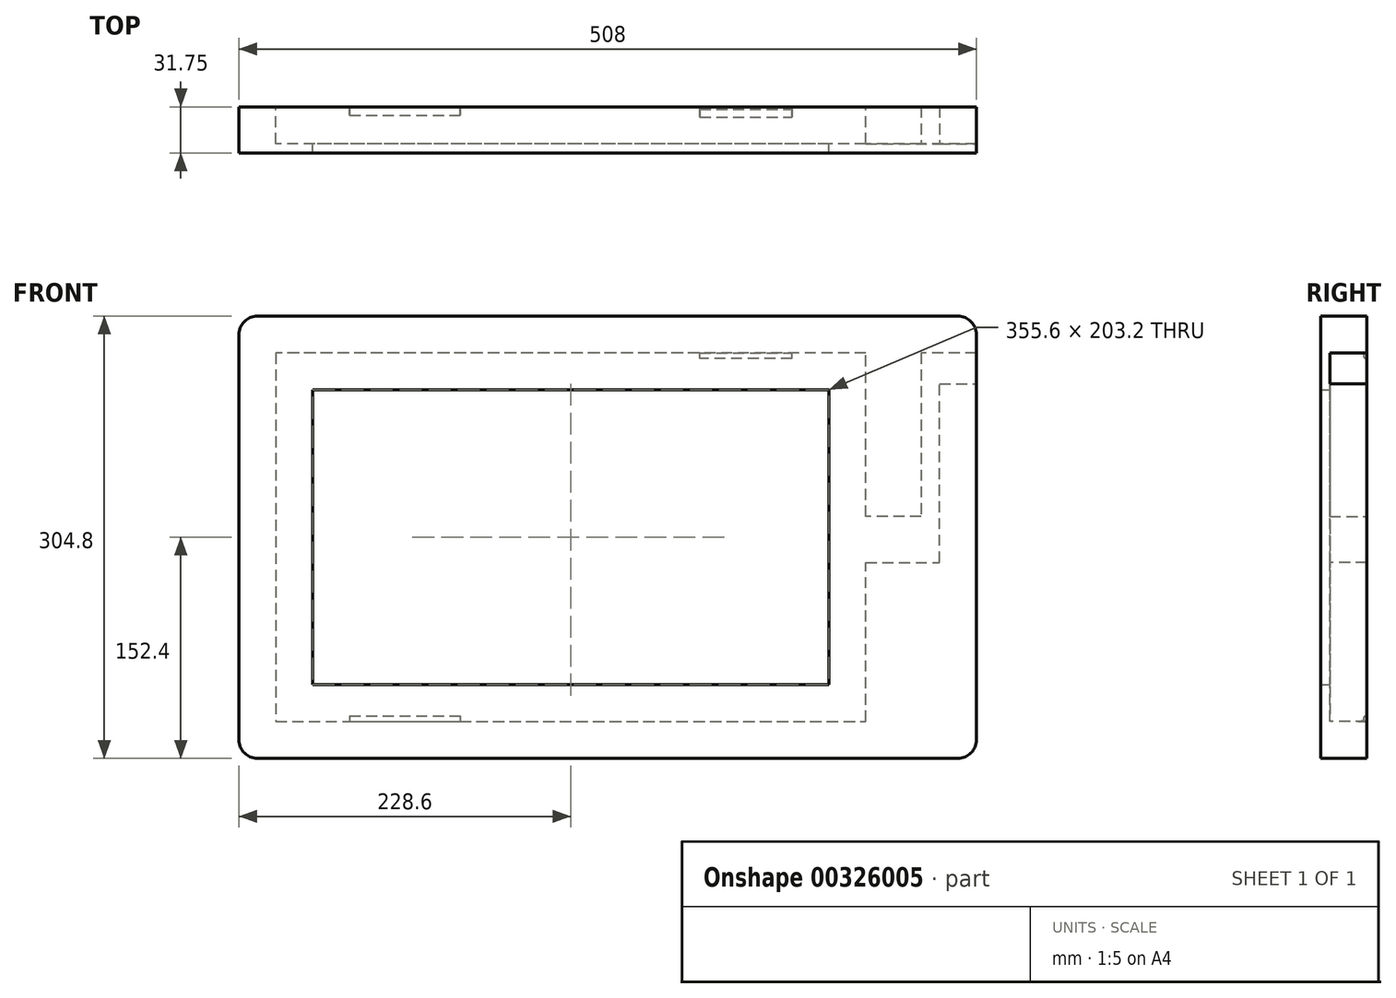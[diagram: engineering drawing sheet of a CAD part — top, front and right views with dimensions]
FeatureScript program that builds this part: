
annotation { "Feature Type Name" : "Feature", "Feature Type Description" : "" }
export const myFeature = defineFeature(function(context is Context, id is Id, definition is map)
    precondition{}
    {
        {
            var Q0;
            Q0=qCreatedBy(makeId("Front.planeOp"),FACE);
            var sketch = newSketch(context, id + "F0", { "sketchPlane" : qUnion([Q0])});
            skLineSegment(sketch, "E0.bottom", {"start": v(177.8, -101.6) * mm, "end": v(-177.8, -101.6) * mm});
            skLineSegment(sketch, "E0.top", {"start": v(177.8, 101.6) * mm, "end": v(-177.8, 101.6) * mm});
            skLineSegment(sketch, "E0.left", {"start": v(177.8, -101.6) * mm, "end": v(177.8, 101.6) * mm});
            skLineSegment(sketch, "E0.right", {"start": v(-177.8, -101.6) * mm, "end": v(-177.8, 101.6) * mm});
            skPoint(sketch, "E0.middle", {"position": v(0, 0) * mm});
            skLineSegment(sketch, "E1.bottom", {"start": v(203.2, 127) * mm, "end": v(-203.2, 127) * mm});
            skLineSegment(sketch, "E1.top", {"start": v(203.2, -127) * mm, "end": v(-203.2, -127) * mm});
            skLineSegment(sketch, "E1.left", {"start": v(203.2, 127) * mm, "end": v(203.2, -127) * mm});
            skLineSegment(sketch, "E1.right", {"start": v(-203.2, 127) * mm, "end": v(-203.2, -127) * mm});
            skLineSegment(sketch, "E2.bottom", {"start": v(279.4, -152.4) * mm, "end": v(-228.6, -152.4) * mm});
            skLineSegment(sketch, "E2.top", {"start": v(279.4, 152.4) * mm, "end": v(-228.6, 152.4) * mm});
            skLineSegment(sketch, "E2.left", {"start": v(279.4, -152.4) * mm, "end": v(279.4, 152.4) * mm});
            skPoint(sketch, "E3.oppositeSnap0", {"position": v(203.2, 0) * mm});
            skLineSegment(sketch, "E3.bottom", {"start": v(241.3, 152.4) * mm, "end": v(254, 152.4) * mm});
            skLineSegment(sketch, "E3.left", {"start": v(241.3, 127) * mm, "end": v(241.3, 14.4) * mm});
            skLineSegment(sketch, "E3.right", {"start": v(254, 105.83) * mm, "end": v(254, 0) * mm});
            skLineSegment(sketch, "E4.bottom", {"start": v(173.05, 14.4) * mm, "end": v(241.3, 14.4) * mm});
            skLineSegment(sketch, "E4.top", {"start": v(173.05, -17.34) * mm, "end": v(254, -17.34) * mm});
            skLineSegment(sketch, "E4.left", {"start": v(173.05, 14.4) * mm, "end": v(173.05, -17.34) * mm});
            skLineSegment(sketch, "E5", {"start": v(254, 0) * mm, "end": v(254, -17.34) * mm});
            skLineSegment(sketch, "E6", {"start": v(241.3, 127) * mm, "end": v(279.4, 127) * mm});
            skLineSegment(sketch, "E7", {"start": v(254, 105.83) * mm, "end": v(279.4, 105.83) * mm});
            skLineSegment(sketch, "E8", {"start": v(-228.6, 152.4) * mm, "end": v(-228.6, -152.4) * mm});
            skPoint(sketch, "E2.right.end.orphan", {"position": v(-279.4, 152.4) * mm});
            skPoint(sketch, "E9.orphan", {"position": v(-279.4, -152.4) * mm});
            skSolve(sketch);
        }
        {
            var Q0;
            {var subQ6=sQuery(id+"F0.wireOp",EDGE,"E1.bottom");Q0=makeQuery(id+"F0.imprint","IMPRINT",FACE,{"disambiguationData":[TD([[makeQuery(id+"F0.imprint","IMPRINT",EDGE,{"derivedFrom":subQ6}),-1.0]])]});}
            var Q1;
            Q1=sQuery(id+"F0.wireOp",EDGE,"E1.right");
            var Q2;
            Q2=sQuery(id+"F0.wireOp",EDGE,"E1.bottom");
            var Q3;
            Q3=sQuery(id+"F0.wireOp",EDGE,"E1.left");
            var Q4;
            Q4=sQuery(id+"F0.wireOp",EDGE,"E1.top");
            var Q5;
            Q5=sQuery(id+"F0.wireOp",EDGE,"E2.bottom");
            var Q6;
            Q6=sQuery(id+"F0.wireOp",EDGE,"E2.right");
            var Q7;
            Q7=sQuery(id+"F0.wireOp",EDGE,"E2.top");
            var Q8;
            Q8=sQuery(id+"F0.wireOp",EDGE,"E2.left");
            extrude(context, id + "F1", {"entities" : qUnion([Q0]), "surfaceEntities" : qUnion([Q1, Q2, Q3, Q4, Q5, Q6, Q7, Q8]), "endBound" : BoundingType.SYMMETRIC, "depth" : 25.4 * mm, "hasDraft" : true, "draftAngle" : 0 * degree});
        }
        {
            var Q0;
            Q0=makeQuery(id+"F1.opExtrude","CAP_FACE",FACE,{"disambiguationData":[OSD([sQuery(id+"F0.wireOp",EDGE,"E1.bottom"),sQuery(id+"F0.wireOp",EDGE,"E1.top"),sQuery(id+"F0.wireOp",EDGE,"E1.left"),sQuery(id+"F0.wireOp",EDGE,"E1.right"),sQuery(id+"F0.wireOp",EDGE,"E2.bottom"),sQuery(id+"F0.wireOp",EDGE,"E2.top"),sQuery(id+"F0.wireOp",EDGE,"E2.left"),sQuery(id+"F0.wireOp",EDGE,"E2.right"),sQuery(id+"F0.wireOp",EDGE,"E3.left"),sQuery(id+"F0.wireOp",EDGE,"E3.right"),sQuery(id+"F0.wireOp",EDGE,"E4.bottom"),sQuery(id+"F0.wireOp",EDGE,"E4.top"),sQuery(id+"F0.wireOp",EDGE,"E5")])],"isStart":false});
            var sketch = newSketch(context, id + "F2", { "sketchPlane" : qUnion([Q0])});
            skLineSegment(sketch, "E10.bottom", {"start": v(279.4, 152.4) * mm, "end": v(-228.6, 152.4) * mm});
            skLineSegment(sketch, "E10.top", {"start": v(279.4, -152.4) * mm, "end": v(-228.6, -152.4) * mm});
            skLineSegment(sketch, "E10.left", {"start": v(279.4, 152.4) * mm, "end": v(279.4, -152.4) * mm});
            skPoint(sketch, "E10.middle", {"position": v(0, 0) * mm});
            skLineSegment(sketch, "E11.bottom", {"start": v(177.8, 101.6) * mm, "end": v(-177.8, 101.6) * mm});
            skLineSegment(sketch, "E11.top", {"start": v(177.8, -101.6) * mm, "end": v(-177.8, -101.6) * mm});
            skLineSegment(sketch, "E11.left", {"start": v(177.8, 101.6) * mm, "end": v(177.8, -101.6) * mm});
            skLineSegment(sketch, "E11.right", {"start": v(-177.8, 101.6) * mm, "end": v(-177.8, -101.6) * mm});
            skLineSegment(sketch, "E12", {"start": v(-228.6, 152.4) * mm, "end": v(-228.6, -152.4) * mm});
            skPoint(sketch, "E10.right.start.orphan", {"position": v(-279.4, 152.4) * mm});
            skPoint(sketch, "E13.orphan", {"position": v(-279.4, -152.4) * mm});
            skSolve(sketch);
        }
        {
            var Q0;
            Q0 = qSketchRegion(id + "F2", true);
            extrude(context, id + "F3", {"entities" : qUnion([Q0]), "operationType" : NewBodyOperationType.ADD, "depth" : 6.35 * mm});
        }
        {
            var Q0;
            {var subQ0=makeQuery(id+"F1.opExtrude","SWEPT_EDGE",EDGE,{"disambiguationData":[OSD([sQuery(id+"F0.wireOp",EDGE,"E2.bottom"),sQuery(id+"F0.wireOp",EDGE,"E2.right")])]});Q0=makeQuery(id+"F3.boolean.opBoolean","MERGE",EDGE,{"derivedFrom":[makeQuery(id+"F1.*.booleanUnion.opBoolean","MERGE",EDGE,{"derivedFrom":[makeQuery(id+"F1.*.split.splitOp","SPLIT",EDGE,{"derivedFrom":subQ0,"isFromBackBody":true}),makeQuery(id+"F1.*.split.splitOp","SPLIT",EDGE,{"derivedFrom":subQ0})]}),makeQuery(id+"F3.opExtrude","SWEPT_EDGE",EDGE,{"disambiguationData":[OSD([sQuery(id+"F2.wireOp",EDGE,"E10.top"),sQuery(id+"F2.wireOp",EDGE,"E10.right")])]})]});}
            var Q1;
            {var subQ0=makeQuery(id+"F1.opExtrude","SWEPT_EDGE",EDGE,{"disambiguationData":[OSD([sQuery(id+"F0.wireOp",EDGE,"E2.top"),sQuery(id+"F0.wireOp",EDGE,"E2.right")])]});Q1=makeQuery(id+"F3.boolean.opBoolean","MERGE",EDGE,{"derivedFrom":[makeQuery(id+"F1.*.booleanUnion.opBoolean","MERGE",EDGE,{"derivedFrom":[makeQuery(id+"F1.*.split.splitOp","SPLIT",EDGE,{"derivedFrom":subQ0,"isFromBackBody":true}),makeQuery(id+"F1.*.split.splitOp","SPLIT",EDGE,{"derivedFrom":subQ0})]}),makeQuery(id+"F3.opExtrude","SWEPT_EDGE",EDGE,{"disambiguationData":[OSD([sQuery(id+"F2.wireOp",EDGE,"E10.bottom"),sQuery(id+"F2.wireOp",EDGE,"E10.right")])]})]});}
            fillet(context, id + "F4", {"entities" : qUnion([Q0, Q1]), "radius" : 12.7 * mm, "tangentPropagation" : true, "allowEdgeOverflow" : false});
        }
        {
            var Q0;
            {var subQ0=makeQuery(id+"F1.opExtrude","SWEPT_FACE",FACE,{"disambiguationData":[OSD([sQuery(id+"F0.wireOp",EDGE,"E1.top")])]});Q0=makeQuery(id+"F1.*.booleanUnion.opBoolean","MERGE",FACE,{"derivedFrom":[makeQuery(id+"F1.*.split.splitOp","SPLIT",FACE,{"derivedFrom":subQ0}),makeQuery(id+"F1.*.split.splitOp","SPLIT",FACE,{"derivedFrom":subQ0,"isFromBackBody":true})]});}
            var sketch = newSketch(context, id + "F5", { "sketchPlane" : qUnion([Q0])});
            skLineSegment(sketch, "E14", {"start": v(-76.2, 12.7) * mm, "end": v(-76.2, -12.7) * mm});
            skLineSegment(sketch, "E15", {"start": v(-152.4, 12.7) * mm, "end": v(-152.4, -12.7) * mm});
            skLineSegment(sketch, "E16", {"start": v(-76.2, -12.7) * mm, "end": v(-152.4, -12.7) * mm});
            skSolve(sketch);
        }
        {
            var Q0;
            {var subQ0=sQuery(id+"F5.wireOp",EDGE,"E14");Q0=makeQuery(id+"F5.imprint","IMPRINT",FACE,{"disambiguationData":[TD([[makeQuery(id+"F5.imprint","IMPRINT",EDGE,{"derivedFrom":subQ0}),-1.0]])]});}
            extrude(context, id + "F6", {"entities" : qUnion([Q0]), "operationType" : NewBodyOperationType.ADD, "depth" : 3.8 * mm, "hasSecondDirection" : true, "secondDirectionOppositeDirection" : true, "secondDirectionDepth" : 25.4 * mm});
        }
        {
            var Q0;
            Q0=makeQuery(id+"F6.opExtrude","SWEPT_FACE",FACE,{"disambiguationData":[OSD([sQuery(id+"F5.wireOp",EDGE,"E14")])]});
            var sketch = newSketch(context, id + "F7", { "sketchPlane" : qUnion([Q0])});
            skFitSpline(sketch, "E17", {"points": [v(12.7, -123.19) * mm, v(10.66, -125.2) * mm, v(-12.7, -127) * mm], "startDerivative": vector(-24.77, 0) * mm, "endDerivative": vector(-87.53, 0) * mm});
            skSolve(sketch);
        }
        {
            var Q0;
            {var subQ1=sQuery(id+"F5.wireOp",EDGE,"E14");var subQ3=makeQuery(id+"F6.opExtrude","CAP_EDGE",EDGE,{"disambiguationData":[OSD([subQ1])],"isStart":false});Q0=makeQuery(id+"F7.imprint","IMPRINT",FACE,{"disambiguationData":[TD([[makeQuery(id+"F7.imprint","IMPRINT",EDGE,{"derivedFrom":subQ3}),1.0]])]});}
            extrude(context, id + "F8", {"entities" : qUnion([Q0]), "operationType" : NewBodyOperationType.REMOVE, "oppositeDirection" : true, "depth" : 87.38 * mm});
        }
        {
            var Q0;
            {var subQ0=makeQuery(id+"F1.opExtrude","SWEPT_FACE",FACE,{"disambiguationData":[OSD([sQuery(id+"F0.wireOp",EDGE,"E1.bottom")])]});Q0=makeQuery(id+"F1.*.booleanUnion.opBoolean","MERGE",FACE,{"derivedFrom":[makeQuery(id+"F1.*.split.splitOp","SPLIT",FACE,{"derivedFrom":subQ0}),makeQuery(id+"F1.*.split.splitOp","SPLIT",FACE,{"derivedFrom":subQ0,"isFromBackBody":true})]});}
            var sketch = newSketch(context, id + "F9", { "sketchPlane" : qUnion([Q0])});
            skLineSegment(sketch, "E18.bottom", {"start": v(88.9, 12.7) * mm, "end": v(152.4, 12.7) * mm});
            skLineSegment(sketch, "E18.left", {"start": v(88.9, 12.7) * mm, "end": v(88.9, -12.7) * mm});
            skLineSegment(sketch, "E18.right", {"start": v(152.4, 12.7) * mm, "end": v(152.4, -12.7) * mm});
            skPoint(sketch, "E18.middle", {"position": v(0, -12.7) * mm});
            skLineSegment(sketch, "E19", {"start": v(152.4, -12.7) * mm, "end": v(88.9, -12.7) * mm});
            skPoint(sketch, "E18.top.end.orphan", {"position": v(152.4, -38.1) * mm});
            skPoint(sketch, "E18.top.start.orphan", {"position": v(88.9, -38.1) * mm});
            skSolve(sketch);
        }
        {
            var Q0;
            Q0 = qSketchRegion(id + "F9", true);
            extrude(context, id + "F10", {"entities" : qUnion([Q0]), "operationType" : NewBodyOperationType.ADD, "depth" : 3.8 * mm});
        }
        {
            var Q0;
            Q0=makeQuery(id+"F10.opExtrude","SWEPT_FACE",FACE,{"disambiguationData":[OSD([sQuery(id+"F9.wireOp",EDGE,"E18.right")])]});
            var sketch = newSketch(context, id + "F11", { "sketchPlane" : qUnion([Q0])});
            skFitSpline(sketch, "E20.MirrorCS", {"points": [v(12.7, 123.2) * mm, v(10.96, 125.11) * mm, v(-12.7, 127) * mm], "startDerivative": vector(-27.14, 0) * mm, "endDerivative": vector(-77.7, 0) * mm});
            skSolve(sketch);
        }
        {
            var Q0;
            {var subQ1=sQuery(id+"F9.wireOp",EDGE,"E18.right");var subQ2=makeQuery(id+"F10.opExtrude","CAP_EDGE",EDGE,{"disambiguationData":[OSD([subQ1])],"isStart":false});Q0=makeQuery(id+"F11.imprint","IMPRINT",FACE,{"disambiguationData":[TD([[makeQuery(id+"F11.imprint","IMPRINT",EDGE,{"derivedFrom":subQ2}),1.0]])]});}
            extrude(context, id + "F12", {"entities" : qUnion([Q0]), "operationType" : NewBodyOperationType.REMOVE, "oppositeDirection" : true, "depth" : 76.2 * mm});
        }
    });
